# Revit family: Damper_Air-BroanNutone-Universal-8in-MD8TU
name_source: partatom
category: Mechanical Equipment
units: mm (PartAtom-declared; Revit-internal decimal feet)

## family parameters
Cut with Voids When Loaded = Yes
Host = Face
OmniClass Number = 23.75.35.17.17
OmniClass Title = Room Air Circulation Fans
Part Type = Normal
Room Calculation Point = No
Round Connector Dimension = Use Radius
Shared = No

## types (1)
- 8in - Damper
    Apparent Load = 0 VA
    Assembly Code = E1090900
    Cover Finish = Metal - Broan NuTone - Stainless Steel
    Default Elevation = 0"
    Description = 8-Inch Universal Automatic Make-Up Air Damper with Pressure Sensor Kit
    Electrical Connector = Electrical Connection
    Exhaust Diameter = 8"
    Exhaust Radius = 4"
    Frequency = 60 Hz
    Length = 10"
    Manufacturer = Broan
    Model = MD8TU
    Number of Poles = 1
    Phase = 1
    Power Factor = 1
    Product Documentation Link = https://www.broan-nutone.com
    Product Name = 8-Inch Universal Automatic Make-Up Air Damper
    Product Page URL = https://www.broan-nutone.com
    Supply Connector = Supply Connection
    URL = https://www.broan-nutone.com
    Voltage = 120 V
    Width = 8"

## geometry (parser evidence)
native form markers: Sweep x2
no freeform markers — native parametric forms only
